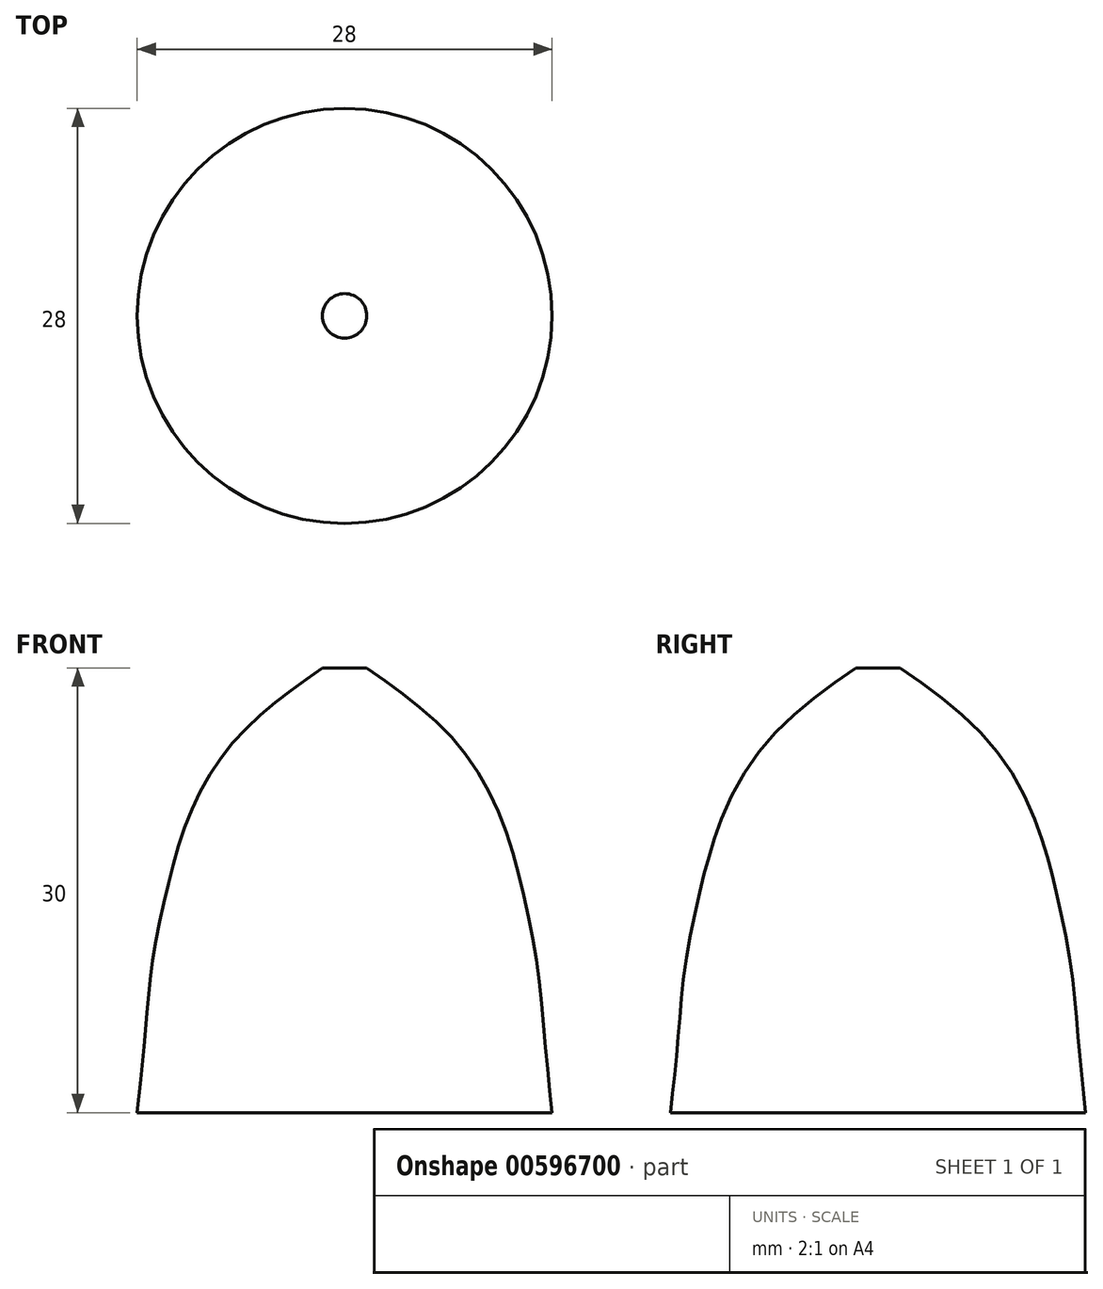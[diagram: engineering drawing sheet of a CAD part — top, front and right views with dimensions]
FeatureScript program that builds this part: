
annotation { "Feature Type Name" : "Feature", "Feature Type Description" : "" }
export const myFeature = defineFeature(function(context is Context, id is Id, definition is map)
    precondition{}
    {
        {
            var Q0;
            Q0=qCreatedBy(makeId("Top.planeOp"),FACE);
            cPlane(context, id + "F0", {"entities" : qUnion([Q0]), "cplaneType" : CPlaneType.OFFSET, "offset" : 5 * mm, "oppositeDirection" : true, "width" : 150 * mm, "height" : 150 * mm});
        }
        {
            var Q0;
            Q0=qCreatedBy(id+"F0.planeOp",FACE);
            var sketch = newSketch(context, id + "F1", { "sketchPlane" : qUnion([Q0])});
            skCircle(sketch, "E0", {"center": v(0, 0) * mm, "radius": 7.5 * mm});
            skSolve(sketch);
        }
        {
            var Q0;
            Q0=qCreatedBy(makeId("Top.planeOp"),FACE);
            var sketch = newSketch(context, id + "F2", { "sketchPlane" : qUnion([Q0])});
            skCircle(sketch, "E1", {"center": v(0, 0) * mm, "radius": 1.5 * mm});
            skSolve(sketch);
        }
        {
            var Q0;
            Q0=qCreatedBy(makeId("Top.planeOp"),FACE);
            cPlane(context, id + "F3", {"entities" : qUnion([Q0]), "cplaneType" : CPlaneType.OFFSET, "offset" : 10 * mm, "oppositeDirection" : true, "width" : 150 * mm, "height" : 150 * mm});
        }
        {
            var Q0;
            Q0=qCreatedBy(id+"F3.planeOp",FACE);
            var sketch = newSketch(context, id + "F4", { "sketchPlane" : qUnion([Q0])});
            skCircle(sketch, "E2", {"center": v(0, 0) * mm, "radius": 10.5 * mm});
            skSolve(sketch);
        }
        {
            var Q0;
            Q0=qCreatedBy(makeId("Top.planeOp"),FACE);
            cPlane(context, id + "F5", {"entities" : qUnion([Q0]), "cplaneType" : CPlaneType.OFFSET, "offset" : 15 * mm, "oppositeDirection" : true, "width" : 150 * mm, "height" : 150 * mm});
        }
        {
            var Q0;
            Q0=qCreatedBy(id+"F5.planeOp",FACE);
            var sketch = newSketch(context, id + "F6", { "sketchPlane" : qUnion([Q0])});
            skCircle(sketch, "E3", {"center": v(0, 0) * mm, "radius": 12 * mm});
            skSolve(sketch);
        }
        {
            var Q0;
            Q0=qCreatedBy(makeId("Top.planeOp"),FACE);
            cPlane(context, id + "F7", {"entities" : qUnion([Q0]), "cplaneType" : CPlaneType.OFFSET, "offset" : 20 * mm, "oppositeDirection" : true, "width" : 150 * mm, "height" : 150 * mm});
        }
        {
            var Q0;
            Q0=qCreatedBy(id+"F7.planeOp",FACE);
            var sketch = newSketch(context, id + "F8", { "sketchPlane" : qUnion([Q0])});
            skCircle(sketch, "E4", {"center": v(0, 0) * mm, "radius": 13 * mm});
            skSolve(sketch);
        }
        {
            var Q0;
            Q0=qCreatedBy(makeId("Top.planeOp"),FACE);
            cPlane(context, id + "F9", {"entities" : qUnion([Q0]), "cplaneType" : CPlaneType.OFFSET, "offset" : 25 * mm, "oppositeDirection" : true, "width" : 150 * mm, "height" : 150 * mm});
        }
        {
            var Q0;
            Q0=qCreatedBy(makeId("Top.planeOp"),FACE);
            cPlane(context, id + "F10", {"entities" : qUnion([Q0]), "cplaneType" : CPlaneType.OFFSET, "offset" : 30 * mm, "oppositeDirection" : true, "width" : 150 * mm, "height" : 150 * mm});
        }
        {
            var Q0;
            Q0=qCreatedBy(id+"F9.planeOp",FACE);
            var sketch = newSketch(context, id + "F11", { "sketchPlane" : qUnion([Q0])});
            skCircle(sketch, "E5", {"center": v(0, 0) * mm, "radius": 13.5 * mm});
            skSolve(sketch);
        }
        {
            var Q0;
            Q0=qCreatedBy(id+"F10.planeOp",FACE);
            var sketch = newSketch(context, id + "F12", { "sketchPlane" : qUnion([Q0])});
            skCircle(sketch, "E6", {"center": v(0, 0) * mm, "radius": 14 * mm});
            skSolve(sketch);
        }
        {
            var Q0;
            Q0=makeQuery(id+"F2.imprint","IMPRINT",FACE,{"disambiguationData":[TD([[makeQuery(id+"F2.imprint","IMPRINT",EDGE,{"derivedFrom":sQuery(id+"F2.wireOp",EDGE,"E1")}),1.0]])]});
            var Q1;
            Q1=makeQuery(id+"F1.imprint","IMPRINT",FACE,{"disambiguationData":[TD([[makeQuery(id+"F1.imprint","IMPRINT",EDGE,{"derivedFrom":sQuery(id+"F1.wireOp",EDGE,"E0")}),1.0]])]});
            var Q2;
            Q2=makeQuery(id+"F4.imprint","IMPRINT",FACE,{"disambiguationData":[TD([[makeQuery(id+"F4.imprint","IMPRINT",EDGE,{"derivedFrom":sQuery(id+"F4.wireOp",EDGE,"E2")}),1.0]])]});
            var Q3;
            Q3=makeQuery(id+"F6.imprint","IMPRINT",FACE,{"disambiguationData":[TD([[makeQuery(id+"F6.imprint","IMPRINT",EDGE,{"derivedFrom":sQuery(id+"F6.wireOp",EDGE,"E3")}),1.0]])]});
            var Q4;
            Q4=makeQuery(id+"F8.imprint","IMPRINT",FACE,{"disambiguationData":[TD([[makeQuery(id+"F8.imprint","IMPRINT",EDGE,{"derivedFrom":sQuery(id+"F8.wireOp",EDGE,"E4")}),1.0]])]});
            var Q5;
            Q5=makeQuery(id+"F11.imprint","IMPRINT",FACE,{"disambiguationData":[TD([[makeQuery(id+"F11.imprint","IMPRINT",EDGE,{"derivedFrom":sQuery(id+"F11.wireOp",EDGE,"E5")}),1.0]])]});
            var Q6;
            Q6=makeQuery(id+"F12.imprint","IMPRINT",FACE,{"disambiguationData":[TD([[makeQuery(id+"F12.imprint","IMPRINT",EDGE,{"derivedFrom":sQuery(id+"F12.wireOp",EDGE,"E6")}),1.0]])]});
            loft(context, id + "F13", {"sheetProfilesArray" : [{ "sheetProfileEntities" : qUnion([Q0]) }, { "sheetProfileEntities" : qUnion([Q1]) }, { "sheetProfileEntities" : qUnion([Q2]) }, { "sheetProfileEntities" : qUnion([Q3]) }, { "sheetProfileEntities" : qUnion([Q4]) }, { "sheetProfileEntities" : qUnion([Q5]) }, { "sheetProfileEntities" : qUnion([Q6]) }]});
        }
    });
